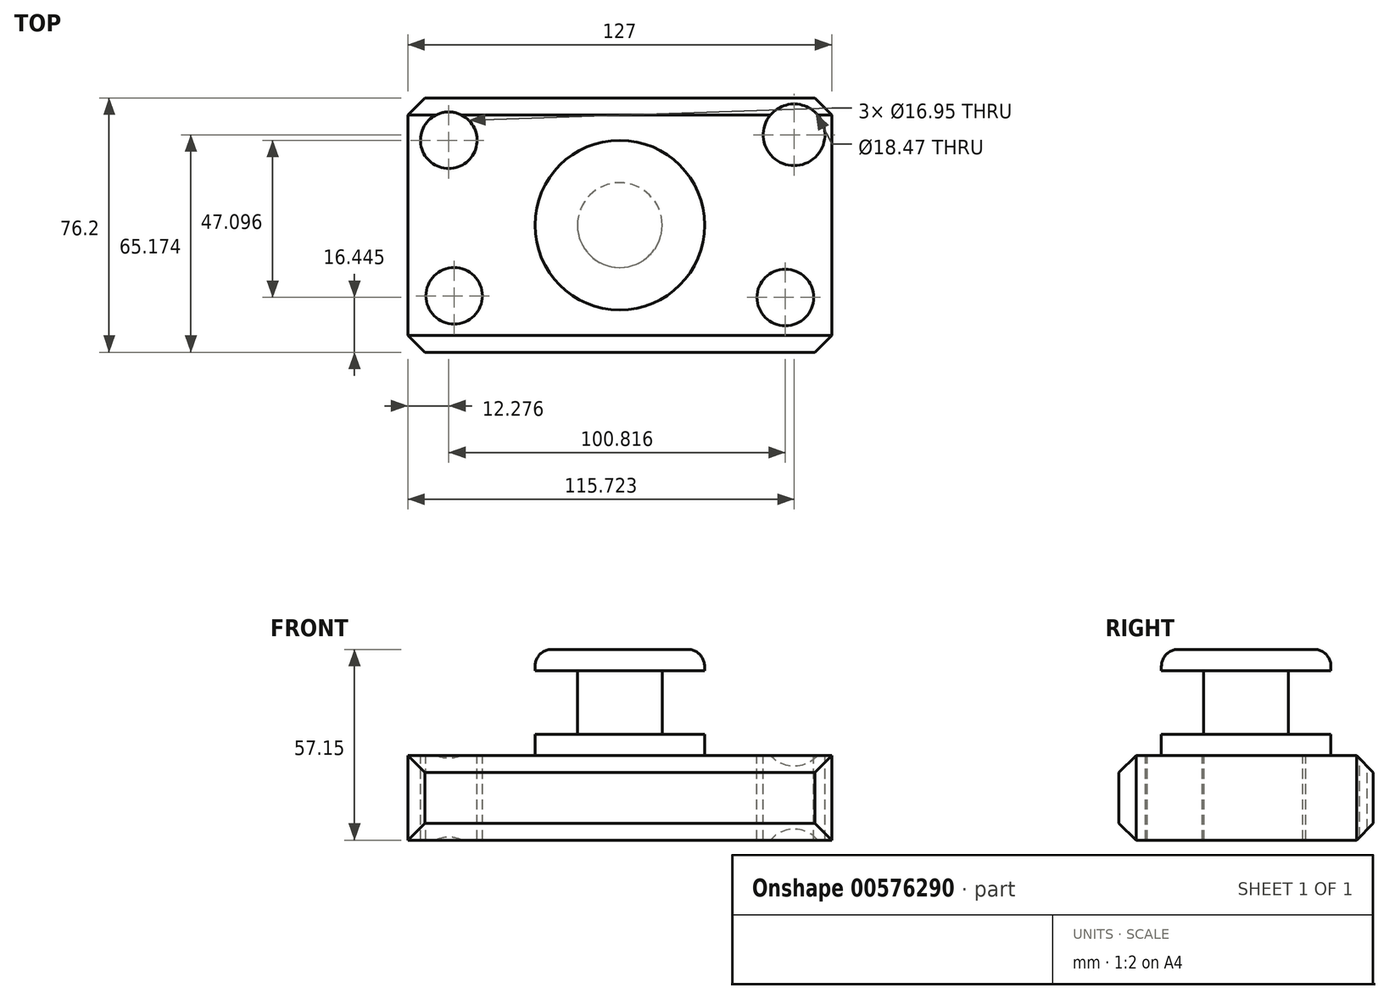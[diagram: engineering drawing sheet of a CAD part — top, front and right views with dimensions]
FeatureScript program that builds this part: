
annotation { "Feature Type Name" : "Feature", "Feature Type Description" : "" }
export const myFeature = defineFeature(function(context is Context, id is Id, definition is map)
    precondition{}
    {
        {
            var Q0;
            Q0=qCreatedBy(makeId("Top.planeOp"),FACE);
            var sketch = newSketch(context, id + "F0", { "sketchPlane" : qUnion([Q0])});
            skLineSegment(sketch, "E0.bottom", {"start": v(63.5, 38.1) * mm, "end": v(-63.5, 38.1) * mm});
            skLineSegment(sketch, "E0.top", {"start": v(63.5, -38.1) * mm, "end": v(-63.5, -38.1) * mm});
            skLineSegment(sketch, "E0.left", {"start": v(63.5, 38.1) * mm, "end": v(63.5, -38.1) * mm});
            skLineSegment(sketch, "E0.right", {"start": v(-63.5, 38.1) * mm, "end": v(-63.5, -38.1) * mm});
            skPoint(sketch, "E0.middle", {"position": v(0, 0) * mm});
            skSolve(sketch);
        }
        {
            var Q0;
            Q0=makeQuery(id+"F0.imprint","IMPRINT",FACE,{"disambiguationData":[TD([[makeQuery(id+"F0.imprint","IMPRINT",EDGE,{"derivedFrom":sQuery(id+"F0.wireOp",EDGE,"E0.bottom")}),1.0]])]});
            extrude(context, id + "F1", {"entities" : qUnion([Q0]), "depth" : 25.4 * mm, "offsetDistance" : 25.4 * mm});
        }
        {
            var Q0;
            Q0=makeQuery(id+"F1.opExtrude","CAP_FACE",FACE,{"disambiguationData":[OSD([sQuery(id+"F0.wireOp",EDGE,"E0.bottom"),sQuery(id+"F0.wireOp",EDGE,"E0.top"),sQuery(id+"F0.wireOp",EDGE,"E0.left"),sQuery(id+"F0.wireOp",EDGE,"E0.right")])],"isStart":false});
            var sketch = newSketch(context, id + "F2", { "sketchPlane" : qUnion([Q0])});
            skCircle(sketch, "E1", {"center": v(-51.22, 25.44) * mm, "radius": 8.48 * mm});
            skPoint(sketch, "E1.first.point", {"position": v(-56.7, 31.9) * mm});
            skPoint(sketch, "E1.second.point", {"position": v(-44.2, 20.7) * mm});
            skPoint(sketch, "E1.third.point", {"position": v(-56.7, 18.97) * mm});
            skCircle(sketch, "E2", {"center": v(-49.62, -21.17) * mm, "radius": 8.48 * mm});
            skCircle(sketch, "E3", {"center": v(52.22, 27.07) * mm, "radius": 9.24 * mm});
            skCircle(sketch, "E4", {"center": v(49.6, -21.65) * mm, "radius": 8.48 * mm});
            skSolve(sketch);
        }
        {
            var Q0;
            Q0 = qSketchRegion(id + "F2", true);
            extrude(context, id + "F3", {"entities" : qUnion([Q0]), "operationType" : NewBodyOperationType.REMOVE, "endBound" : BoundingType.THROUGH_ALL, "oppositeDirection" : true, "depth" : 25.4 * mm, "offsetDistance" : 25.4 * mm});
        }
        {
            var Q0;
            Q0=qCreatedBy(makeId("Front.planeOp"),FACE);
            var sketch = newSketch(context, id + "F4", { "sketchPlane" : qUnion([Q0])});
            skLineSegment(sketch, "E5.bottom", {"start": v(0, 25.4) * mm, "end": v(12.7, 25.4) * mm});
            skLineSegment(sketch, "E5.top", {"start": v(0, 50.8) * mm, "end": v(12.7, 50.8) * mm});
            skLineSegment(sketch, "E5.left", {"start": v(0, 25.4) * mm, "end": v(0, 50.8) * mm});
            skLineSegment(sketch, "E5.right", {"start": v(12.7, 25.4) * mm, "end": v(12.7, 50.8) * mm});
            skSolve(sketch);
        }
        {
            var Q0;
            Q0=makeQuery(id+"F4.imprint","IMPRINT",FACE,{"disambiguationData":[TD([[makeQuery(id+"F4.imprint","IMPRINT",EDGE,{"derivedFrom":sQuery(id+"F4.wireOp",EDGE,"E5.bottom")}),1.0]])]});
            var Q1;
            Q1=sQuery(id+"F4.wireOp",EDGE,"E5.left");
            revolve(context, id + "F5", {"operationType" : NewBodyOperationType.ADD, "entities" : qUnion([Q0]), "axis" : qUnion([Q1]), "revolveType" : RevolveType.FULL});
        }
        {
            var Q0;
            Q0=qCreatedBy(makeId("Front.planeOp"),FACE);
            var sketch = newSketch(context, id + "F6", { "sketchPlane" : qUnion([Q0])});
            skLineSegment(sketch, "E6.bottom", {"start": v(0, 57.15) * mm, "end": v(25.4, 57.15) * mm});
            skLineSegment(sketch, "E6.top", {"start": v(0, 50.8) * mm, "end": v(25.4, 50.8) * mm});
            skLineSegment(sketch, "E6.left", {"start": v(0, 57.15) * mm, "end": v(0, 50.8) * mm});
            skLineSegment(sketch, "E6.right", {"start": v(25.4, 57.15) * mm, "end": v(25.4, 50.8) * mm});
            skSolve(sketch);
        }
        {
            var Q0;
            Q0=makeQuery(id+"F6.imprint","IMPRINT",FACE,{"disambiguationData":[TD([[makeQuery(id+"F6.imprint","IMPRINT",EDGE,{"derivedFrom":sQuery(id+"F6.wireOp",EDGE,"E6.bottom")}),-1.0]])]});
            var Q1;
            Q1=sQuery(id+"F6.wireOp",EDGE,"E6.left");
            revolve(context, id + "F7", {"operationType" : NewBodyOperationType.ADD, "entities" : qUnion([Q0]), "axis" : qUnion([Q1]), "revolveType" : RevolveType.FULL});
        }
        {
            var Q0;
            Q0=qCreatedBy(makeId("Front.planeOp"),FACE);
            var sketch = newSketch(context, id + "F8", { "sketchPlane" : qUnion([Q0])});
            skLineSegment(sketch, "E7.bottom", {"start": v(0, 31.75) * mm, "end": v(25.4, 31.75) * mm});
            skLineSegment(sketch, "E7.top", {"start": v(0, 25.4) * mm, "end": v(25.4, 25.4) * mm});
            skLineSegment(sketch, "E7.left", {"start": v(0, 31.75) * mm, "end": v(0, 25.4) * mm});
            skLineSegment(sketch, "E7.right", {"start": v(25.4, 31.75) * mm, "end": v(25.4, 25.4) * mm});
            skSolve(sketch);
        }
        {
            var Q0;
            Q0 = qSketchRegion(id + "F8", true);
            var Q1;
            Q1=sQuery(id+"F8.wireOp",EDGE,"E7.left");
            revolve(context, id + "F9", {"operationType" : NewBodyOperationType.ADD, "entities" : qUnion([Q0]), "axis" : qUnion([Q1]), "revolveType" : RevolveType.FULL});
        }
        {
            var Q0;
            Q0=makeQuery(id+"F7.opRevolve","SWEPT_FACE",FACE,{"disambiguationData":[OSD([sQuery(id+"F6.wireOp",EDGE,"E6.bottom")])]});
            var Q1;
            Q1=makeQuery(id+"F9.opRevolve","SWEPT_EDGE",EDGE,{"disambiguationData":[OSD([sQuery(id+"F8.wireOp",EDGE,"E7.top"),sQuery(id+"F8.wireOp",EDGE,"E7.right")])]});
            fillet(context, id + "F10", {"entities" : qUnion([Q0, Q1]), "radius" : 5.08 * mm, "tangentPropagation" : true, "allowEdgeOverflow" : false});
        }
        {
            var Q0;
            Q0=makeQuery(id+"F1.opExtrude","SWEPT_FACE",FACE,{"disambiguationData":[OSD([sQuery(id+"F0.wireOp",EDGE,"E0.top")])]});
            var Q1;
            Q1=makeQuery(id+"F1.opExtrude","SWEPT_FACE",FACE,{"disambiguationData":[OSD([sQuery(id+"F0.wireOp",EDGE,"E0.bottom")])]});
            chamfer(context, id + "F11", {"entities" : qUnion([Q0, Q1]), "width" : 5.08 * mm, "tangentPropagation" : true});
        }
    });
